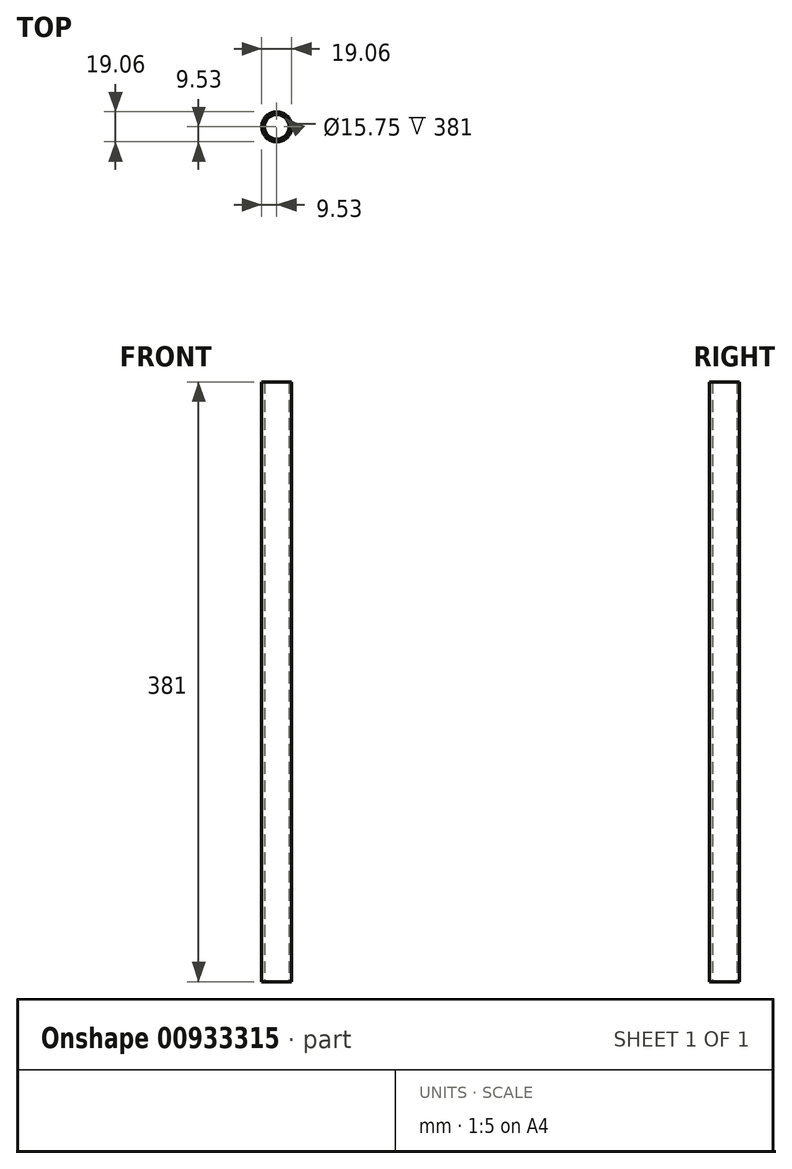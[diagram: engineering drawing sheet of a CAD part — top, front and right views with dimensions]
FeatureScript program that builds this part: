
annotation { "Feature Type Name" : "Feature", "Feature Type Description" : "" }
export const myFeature = defineFeature(function(context is Context, id is Id, definition is map)
    precondition{}
    {
        {
            var Q0;
            Q0=qCreatedBy(makeId("Top.planeOp"),FACE);
            var sketch = newSketch(context, id + "F0", { "sketchPlane" : qUnion([Q0])});
            skCircle(sketch, "E0", {"center": v(0, 0) * mm, "radius": 9.53 * mm});
            skCircle(sketch, "E1", {"center": v(0, 0) * mm, "radius": 7.87 * mm});
            skSolve(sketch);
        }
        {
            var Q0;
            Q0=makeQuery(id+"F0.imprint","IMPRINT",FACE,{"disambiguationData":[TD([[makeQuery(id+"F0.imprint","IMPRINT",EDGE,{"derivedFrom":sQuery(id+"F0.wireOp",EDGE,"E0")}),1.0]])]});
            extrude(context, id + "F1", {"entities" : qUnion([Q0]), "depth" : 381 * mm, "offsetDistance" : 25.4 * mm});
        }
    });
